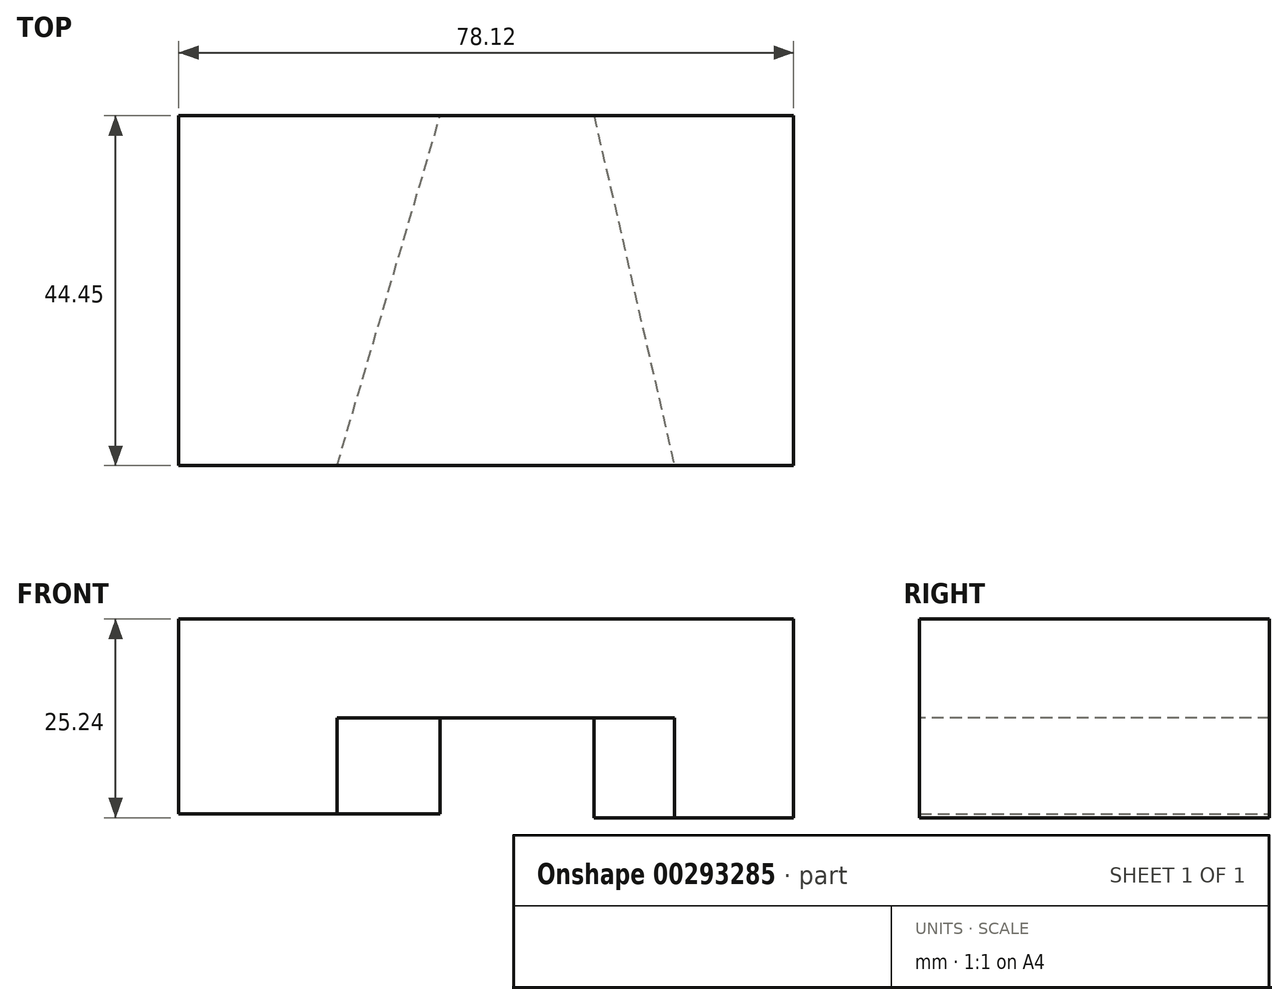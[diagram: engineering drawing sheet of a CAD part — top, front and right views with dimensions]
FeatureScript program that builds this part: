
annotation { "Feature Type Name" : "Feature", "Feature Type Description" : "" }
export const myFeature = defineFeature(function(context is Context, id is Id, definition is map)
    precondition{}
    {
        {
            var Q0;
            Q0=qCreatedBy(makeId("Front.planeOp"),FACE);
            var sketch = newSketch(context, id + "F0", { "sketchPlane" : qUnion([Q0])});
            skLineSegment(sketch, "E0", {"start": v(-58.59, 43.87) * mm, "end": v(-58.59, 31.33) * mm});
            skLineSegment(sketch, "E1", {"start": v(-58.59, 31.33) * mm, "end": v(19.53, 31.33) * mm});
            skLineSegment(sketch, "E2", {"start": v(19.53, 31.33) * mm, "end": v(19.53, 43.87) * mm});
            skLineSegment(sketch, "E3", {"start": v(19.53, 43.87) * mm, "end": v(-58.59, 43.87) * mm});
            skSolve(sketch);
        }
        {
            var Q0;
            Q0=makeQuery(id+"F0.imprint","IMPRINT",FACE,{"disambiguationData":[TD([[makeQuery(id+"F0.imprint","IMPRINT",EDGE,{"derivedFrom":sQuery(id+"F0.wireOp",EDGE,"E0")}),1.0]])]});
            extrude(context, id + "F1", {"entities" : qUnion([Q0]), "depth" : 44.45 * mm});
        }
        {
            var Q0;
            Q0=makeQuery(id+"F1.opExtrude","SWEPT_FACE",FACE,{"disambiguationData":[OSD([sQuery(id+"F0.wireOp",EDGE,"E1")])]});
            var sketch = newSketch(context, id + "F2", { "sketchPlane" : qUnion([Q0])});
            skLineSegment(sketch, "E4", {"start": v(-38.47, 44.45) * mm, "end": v(-25.36, 0) * mm});
            skSolve(sketch);
        }
        {
            var Q0;
            {var subQ0=sQuery(id+"F2.wireOp",EDGE,"E4");Q0=makeQuery(id+"F2.imprint","IMPRINT",FACE,{"disambiguationData":[TD([[makeQuery(id+"F2.imprint","IMPRINT",EDGE,{"derivedFrom":subQ0}),-1.0]])]});}
            extrude(context, id + "F3", {"entities" : qUnion([Q0]), "operationType" : NewBodyOperationType.ADD, "depth" : 12.2 * mm});
        }
        {
            var Q0;
            Q0=makeQuery(id+"F1.opExtrude","SWEPT_FACE",FACE,{"disambiguationData":[OSD([sQuery(id+"F0.wireOp",EDGE,"E1")])]});
            var sketch = newSketch(context, id + "F4", { "sketchPlane" : qUnion([Q0])});
            skLineSegment(sketch, "E5", {"start": v(-5.83, 0) * mm, "end": v(4.37, 44.45) * mm});
            skSolve(sketch);
        }
        {
            var Q0;
            Q0 = qSketchRegion(id + "F4", true);
            var Q1;
            {var subQ0=sQuery(id+"F4.wireOp",EDGE,"E5");Q1=makeQuery(id+"F4.imprint","IMPRINT",FACE,{"disambiguationData":[TD([[makeQuery(id+"F4.imprint","IMPRINT",EDGE,{"derivedFrom":subQ0}),-1.0]])]});}
            extrude(context, id + "F5", {"entities" : qUnion([Q0, Q1]), "operationType" : NewBodyOperationType.ADD, "depth" : 12.7 * mm});
        }
    });
